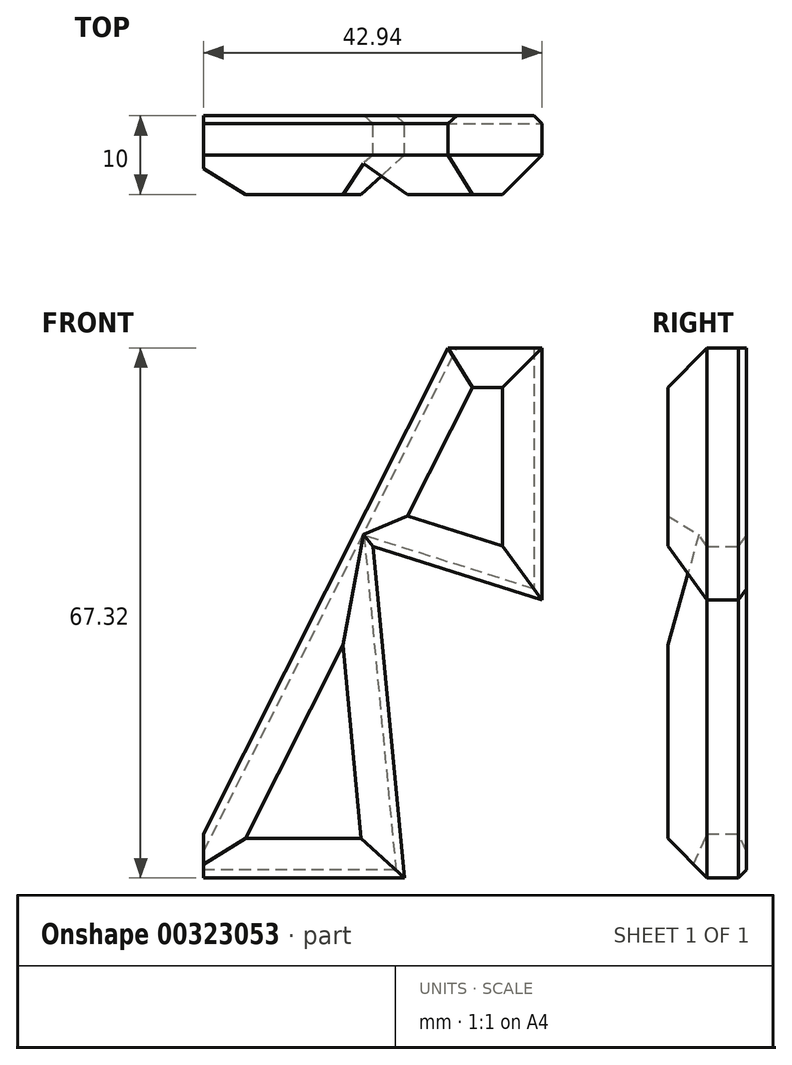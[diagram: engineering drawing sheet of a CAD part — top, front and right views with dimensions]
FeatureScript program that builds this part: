
annotation { "Feature Type Name" : "Feature", "Feature Type Description" : "" }
export const myFeature = defineFeature(function(context is Context, id is Id, definition is map)
    precondition{}
    {
        {
            var Q0;
            Q0=qCreatedBy(makeId("Front.planeOp"),FACE);
            var sketch = newSketch(context, id + "F0", { "sketchPlane" : qUnion([Q0])});
            skLineSegment(sketch, "E0", {"start": v(0, -31.13) * mm, "end": v(25.5, -31.13) * mm});
            skLineSegment(sketch, "E1", {"start": v(25.5, -31.13) * mm, "end": v(21.49, 10.98) * mm});
            skLineSegment(sketch, "E2", {"start": v(21.49, 10.98) * mm, "end": v(42.94, 4.19) * mm});
            skLineSegment(sketch, "E3", {"start": v(42.94, 4.19) * mm, "end": v(42.94, 36.19) * mm});
            skLineSegment(sketch, "E4", {"start": v(42.94, 36.19) * mm, "end": v(31.04, 36.19) * mm});
            skLineSegment(sketch, "E5", {"start": v(31.04, 36.19) * mm, "end": v(0, -25.55) * mm});
            skLineSegment(sketch, "E6", {"start": v(0, -25.55) * mm, "end": v(0, -31.13) * mm, "construction": true});
            skLineSegment(sketch, "E7", {"start": v(0, -25.55) * mm, "end": v(0, -31.13) * mm});
            skSolve(sketch);
        }
        {
            var Q0;
            Q0 = qSketchRegion(id + "F0", true);
            extrude(context, id + "F1", {"entities" : qUnion([Q0]), "depth" : 10 * mm});
        }
        {
            var Q0;
            Q0=makeQuery(id+"F1.opExtrude","CAP_FACE",FACE,{"disambiguationData":[OSD([sQuery(id+"F0.wireOp",EDGE,"E0"),sQuery(id+"F0.wireOp",EDGE,"E1"),sQuery(id+"F0.wireOp",EDGE,"E2"),sQuery(id+"F0.wireOp",EDGE,"E3"),sQuery(id+"F0.wireOp",EDGE,"E4"),sQuery(id+"F0.wireOp",EDGE,"E5"),sQuery(id+"F0.wireOp",EDGE,"E7")])],"isStart":false});
            var Q1;
            Q1=makeQuery(id+"F1.opExtrude","CAP_EDGE",EDGE,{"disambiguationData":[OSD([sQuery(id+"F0.wireOp",EDGE,"E3")])],"isStart":false});
            var Q2;
            Q2=makeQuery(id+"F1.opExtrude","CAP_EDGE",EDGE,{"disambiguationData":[OSD([sQuery(id+"F0.wireOp",EDGE,"E5")])],"isStart":false});
            var Q3;
            Q3=makeQuery(id+"F1.opExtrude","CAP_EDGE",EDGE,{"disambiguationData":[OSD([sQuery(id+"F0.wireOp",EDGE,"E2")])],"isStart":false});
            var Q4;
            Q4=makeQuery(id+"F1.opExtrude","CAP_EDGE",EDGE,{"disambiguationData":[OSD([sQuery(id+"F0.wireOp",EDGE,"E1")])],"isStart":false});
            var Q5;
            Q5=makeQuery(id+"F1.opExtrude","CAP_EDGE",EDGE,{"disambiguationData":[OSD([sQuery(id+"F0.wireOp",EDGE,"E0")])],"isStart":false});
            chamfer(context, id + "F2", {"entities" : qUnion([Q0, Q1, Q2, Q3, Q4, Q5]), "width" : 5 * mm, "tangentPropagation" : true});
        }
        {
            var Q0;
            Q0=makeQuery(id+"F1.opExtrude","CAP_EDGE",EDGE,{"disambiguationData":[OSD([sQuery(id+"F0.wireOp",EDGE,"E3")])],"isStart":false});
            var Q1;
            Q1=makeQuery(id+"F1.opExtrude","CAP_EDGE",EDGE,{"disambiguationData":[OSD([sQuery(id+"F0.wireOp",EDGE,"E2")])],"isStart":false});
            var Q2;
            Q2=makeQuery(id+"F1.opExtrude","CAP_EDGE",EDGE,{"disambiguationData":[OSD([sQuery(id+"F0.wireOp",EDGE,"E1")])],"isStart":false});
            var Q3;
            Q3=makeQuery(id+"F1.opExtrude","CAP_EDGE",EDGE,{"disambiguationData":[OSD([sQuery(id+"F0.wireOp",EDGE,"E0")])],"isStart":false});
            var Q4;
            Q4=makeQuery(id+"F1.opExtrude","CAP_EDGE",EDGE,{"disambiguationData":[OSD([sQuery(id+"F0.wireOp",EDGE,"E5")])],"isStart":false});
            var Q5;
            Q5=makeQuery(id+"F1.opExtrude","CAP_EDGE",EDGE,{"disambiguationData":[OSD([sQuery(id+"F0.wireOp",EDGE,"E0")])],"isStart":true});
            chamfer(context, id + "F3", {"entities" : qUnion([Q0, Q1, Q2, Q3, Q4, Q5]), "width" : 1 * mm, "tangentPropagation" : true});
        }
        {
            var Q0;
            Q0=makeQuery(id+"F1.opExtrude","CAP_EDGE",EDGE,{"disambiguationData":[OSD([sQuery(id+"F0.wireOp",EDGE,"E1")])],"isStart":true});
            var Q1;
            Q1=makeQuery(id+"F1.opExtrude","CAP_EDGE",EDGE,{"disambiguationData":[OSD([sQuery(id+"F0.wireOp",EDGE,"E2")])],"isStart":true});
            var Q2;
            Q2=makeQuery(id+"F1.opExtrude","CAP_EDGE",EDGE,{"disambiguationData":[OSD([sQuery(id+"F0.wireOp",EDGE,"E3")])],"isStart":true});
            var Q3;
            Q3=makeQuery(id+"F1.opExtrude","CAP_EDGE",EDGE,{"disambiguationData":[OSD([sQuery(id+"F0.wireOp",EDGE,"E5")])],"isStart":true});
            chamfer(context, id + "F4", {"entities" : qUnion([Q0, Q1, Q2, Q3]), "width" : 1 * mm, "tangentPropagation" : true});
        }
    });
